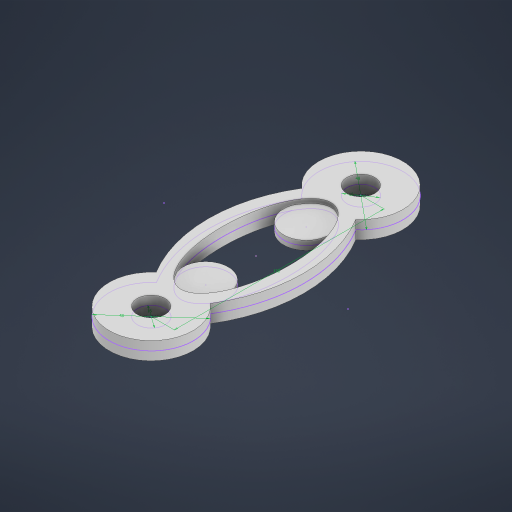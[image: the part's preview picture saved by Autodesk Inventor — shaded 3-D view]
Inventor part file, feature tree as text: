
AUTODESK INVENTOR PART (.ipt)
format: ipt  version: 2024.3 (Build 283343000, 343)  size: 222,720 bytes
history: native  units: mm
features: extrude x2, sketch x1
ambient origin geometry x8: Origin, YZ Plane, XZ Plane, XY Plane, X Axis, Y Axis, Z Axis, Center Point
bodies: Body1 (feature_tree)
feature tree (3):
  sketch  "Sketch1"  dims[d0=16.0mm d1=16.0mm d2=120.0mm d4=48.0mm d5=48.0mm d24=10.0mm d25=0.0mm d26=5.0mm d27=0.0mm d20=0.872665mm d21=0.872665mm d22=0.5mm d23=0.872665mm]
  extrude  "Extrusion4"  Depth=5.0mm
  extrude  "Extrusion5"  Depth=5.0mm
